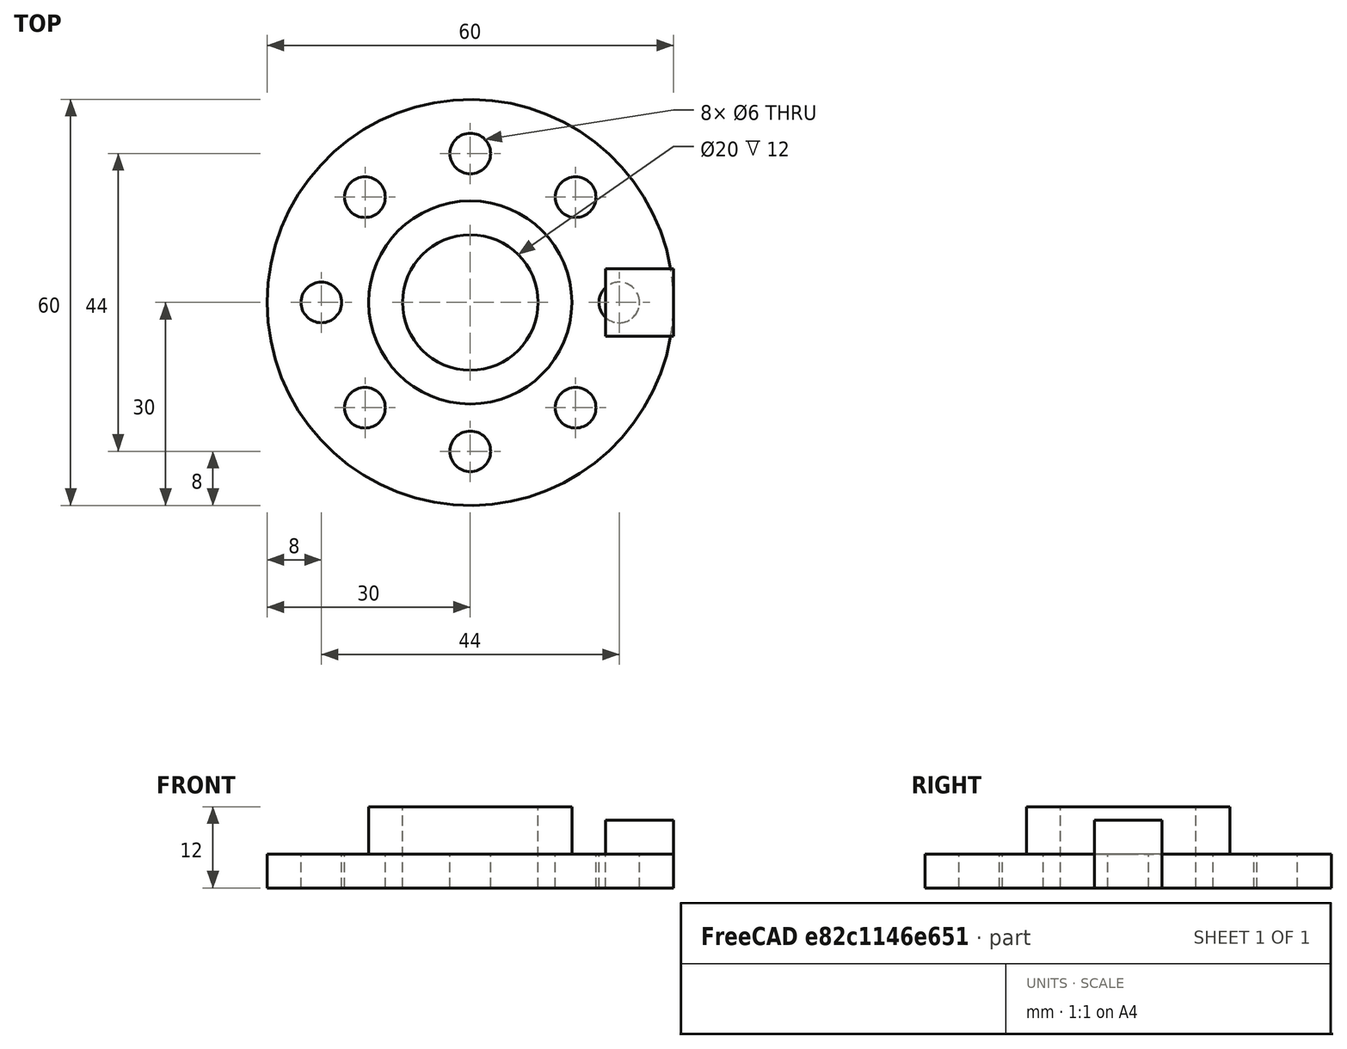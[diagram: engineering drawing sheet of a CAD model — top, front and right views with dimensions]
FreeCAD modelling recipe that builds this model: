
FCSTD DOCUMENT  (FreeCAD 0.16R6707 (Git))
Label: Brida
License: CreativeCommons Attribution-ShareAlike
LicenseURL: http://creativecommons.org/licenses/by-sa/4.0/
objects: Part::Cylinder×4, Part::Cut×2, Part::Box×1, Part::MultiFuse×1, Part::FeaturePython×1
note: 9 computed .brp shape members not serialized (recipe doc carries the construction recipe); baked Part::Feature solids carry a one-line shape summary decoded from their .brp

FEATURE [Part::Box] Box  label="master_cube"
  Height = 10
  Length = 10
  Placement = pos=(20,-5,0) rot=(0,0,1;0rad)
  Width = 10
FEATURE [Part::Cylinder] Cylinder  label="Base_brida"
  Angle = 360
  Height = 5
  Radius = 30
FEATURE [Part::Cylinder] Cylinder001  label="Tubo_exterior"
  Angle = 360
  Height = 12
  Radius = 15
FEATURE [Part::MultiFuse] Fusion  label="Brida"
  Shapes = -> [Cylinder,Cylinder001]
FEATURE [Part::Cylinder] Cylinder002  label="Tubointerior"
  Angle = 360
  Height = 30
  Radius = 10
FEATURE [Part::Cut] Cut  label="Brida_sin_taladros"
  Base = -> Fusion
  Tool = -> Cylinder002
FEATURE [Part::Cylinder] Cylinder003  label="taladro_master"
  Angle = 360
  Height = 14
  Placement = pos=(22,0,0) rot=(0,0,1;0rad)
  Radius = 3
FEATURE [Part::FeaturePython] Array001  label="Taladros"  # Draft array (typed FeaturePython)
  Angle = 360
  ArrayType = 1
  Axis = (0,0,1)
  Base = -> Cylinder003
  Center = (0,0,0)
  Fuse = false
  IntervalAxis = (0,0,0)
  IntervalX = (1,0,0)
  IntervalY = (0,1,0)
  IntervalZ = (0,0,0)
  NumberPolar = 8
  NumberX = 2
  NumberY = 2
  NumberZ = 1
FEATURE [Part::Cut] Cut001  label="Brida_completa"
  Base = -> Cut
  Tool = -> Array001
